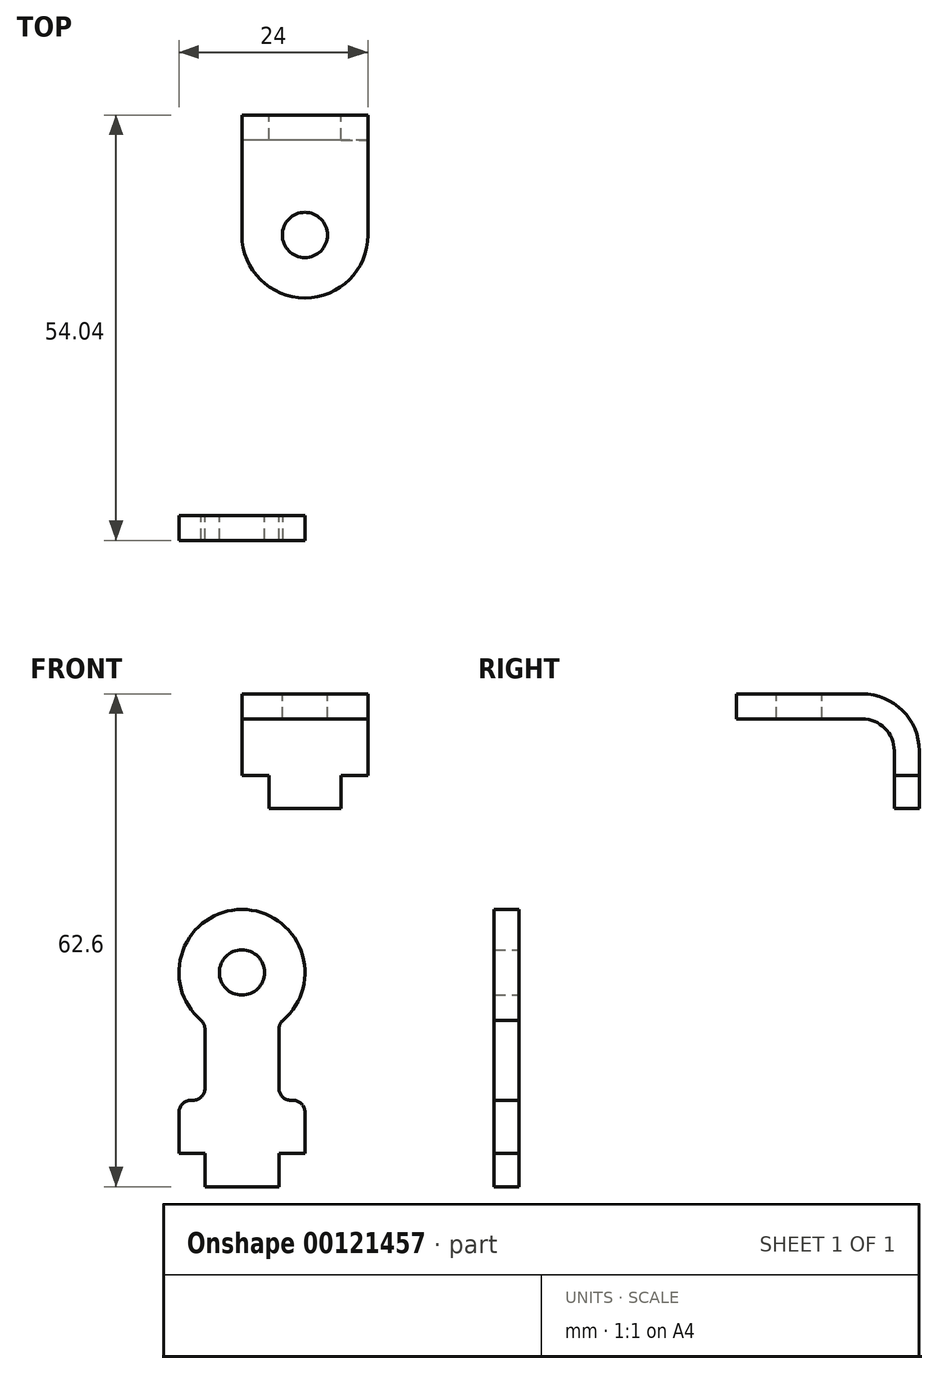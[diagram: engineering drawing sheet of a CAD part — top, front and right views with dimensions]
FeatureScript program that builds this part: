
annotation { "Feature Type Name" : "Feature", "Feature Type Description" : "" }
export const myFeature = defineFeature(function(context is Context, id is Id, definition is map)
    precondition{}
    {
        {
            var Q0;
            Q0=qCreatedBy(makeId("Front.planeOp"),FACE);
            var sketch = newSketch(context, id + "F0", { "sketchPlane" : qUnion([Q0])});
            skCircle(sketch, "E0", {"center": v(0, 0) * mm, "radius": 2.87 * mm});
            skLineSegment(sketch, "E1", {"start": v(-4.7, -7.2) * mm, "end": v(-4.7, -14.72) * mm});
            skLineSegment(sketch, "E2", {"start": v(-6.22, -16.24) * mm, "end": v(-6.48, -16.24) * mm});
            skLineSegment(sketch, "E3", {"start": v(-8, -17.77) * mm, "end": v(-8, -22.99) * mm});
            skLineSegment(sketch, "E4", {"start": v(-8, -22.99) * mm, "end": v(-4.7, -22.99) * mm});
            skLineSegment(sketch, "E5", {"start": v(-4.7, -22.99) * mm, "end": v(-4.7, -27.2) * mm});
            skLineSegment(sketch, "E6", {"start": v(-4.7, -27.2) * mm, "end": v(0, -27.2) * mm});
            skLineSegment(sketch, "E7", {"start": v(-4.7, -7.2) * mm, "end": v(4.7, -7.2) * mm, "construction": true});
            skPoint(sketch, "E8.visualSharp", {"position": v(-4.7, -16.24) * mm});
            skArc(sketch, "E8.filletArc", {"start": v(-6.22, -16.24) * mm, "mid": v(-5.15, -15.8) * mm, "end": v(-4.7, -14.72) * mm});
            skPoint(sketch, "E9.visualSharp", {"position": v(-8, -16.24) * mm});
            skArc(sketch, "E9.filletArc", {"start": v(-6.48, -16.24) * mm, "mid": v(-7.55, -16.69) * mm, "end": v(-8, -17.77) * mm});
            skPoint(sketch, "E10.visualSharp", {"position": v(-4.7, -6.47) * mm});
            skArc(sketch, "E10.filletArc", {"start": v(-4.7, -7.2) * mm, "mid": v(-4.83, -6.59) * mm, "end": v(-5.2, -6.07) * mm});
            skLineSegment(sketch, "E11", {"start": v(-4.7, -14.72) * mm, "end": v(4.7, -14.72) * mm, "construction": true});
            skArc(sketch, "E12.MirrorCS", {"start": v(4.7, -7.2) * mm, "mid": v(4.83, -6.59) * mm, "end": v(5.2, -6.07) * mm});
            skLineSegment(sketch, "E13.MirrorCS", {"start": v(4.7, -7.2) * mm, "end": v(4.7, -14.72) * mm});
            skArc(sketch, "E14.MirrorCS", {"start": v(6.22, -16.24) * mm, "mid": v(5.15, -15.8) * mm, "end": v(4.7, -14.72) * mm});
            skLineSegment(sketch, "E15.MirrorCS", {"start": v(6.22, -16.24) * mm, "end": v(6.48, -16.24) * mm});
            skArc(sketch, "E16.MirrorCS", {"start": v(6.48, -16.24) * mm, "mid": v(7.55, -16.69) * mm, "end": v(8, -17.77) * mm});
            skLineSegment(sketch, "E17.MirrorCS", {"start": v(8, -17.77) * mm, "end": v(8, -22.99) * mm});
            skLineSegment(sketch, "E18.MirrorCS", {"start": v(8, -22.99) * mm, "end": v(4.7, -22.99) * mm});
            skLineSegment(sketch, "E19.MirrorCS", {"start": v(4.7, -22.99) * mm, "end": v(4.7, -27.2) * mm});
            skLineSegment(sketch, "E20.MirrorCS", {"start": v(4.7, -27.2) * mm, "end": v(0, -27.2) * mm});
            skArc(sketch, "E21.trimOffspring", {"start": v(5.2, -6.07) * mm, "mid": v(0, 8) * mm, "end": v(-5.2, -6.07) * mm});
            skSolve(sketch);
        }
        {
            var Q0;
            Q0 = qSketchRegion(id + "F0", true);
            extrude(context, id + "F1", {"entities" : qUnion([Q0]), "depth" : 3.17 * mm});
        }
        {
            var Q0;
            Q0=qCreatedBy(makeId("Right.planeOp"),FACE);
            var sketch = newSketch(context, id + "F2", { "sketchPlane" : qUnion([Q0])});
            skLineSegment(sketch, "E22", {"start": v(50.86, 20.82) * mm, "end": v(47.68, 20.82) * mm});
            skLineSegment(sketch, "E23", {"start": v(47.68, 20.82) * mm, "end": v(47.68, 28.15) * mm});
            skLineSegment(sketch, "E24", {"start": v(43.62, 32.22) * mm, "end": v(27.62, 32.22) * mm});
            skLineSegment(sketch, "E25", {"start": v(27.62, 32.22) * mm, "end": v(27.62, 35.4) * mm});
            skLineSegment(sketch, "E26", {"start": v(27.62, 35.4) * mm, "end": v(43.62, 35.4) * mm});
            skLineSegment(sketch, "E27", {"start": v(50.86, 20.82) * mm, "end": v(50.86, 28.15) * mm});
            skPoint(sketch, "E28.visualSharp", {"position": v(47.68, 32.22) * mm});
            skArc(sketch, "E28.filletArc", {"start": v(47.68, 28.15) * mm, "mid": v(46.5, 31.02) * mm, "end": v(43.62, 32.22) * mm});
            skPoint(sketch, "E29.newPointA", {"position": v(50.86, 32.22) * mm});
            skPoint(sketch, "E29.newPointB", {"position": v(47.68, 35.4) * mm});
            skArc(sketch, "E29.filletArc", {"start": v(50.86, 28.15) * mm, "mid": v(48.74, 33.27) * mm, "end": v(43.62, 35.4) * mm});
            skSolve(sketch);
        }
        {
            var Q0;
            Q0=makeQuery(id+"F2.imprint","IMPRINT",FACE,{"disambiguationData":[TD([[makeQuery(id+"F2.imprint","IMPRINT",EDGE,{"derivedFrom":sQuery(id+"F2.wireOp",EDGE,"E22")}),-1.0]])]});
            extrude(context, id + "F3", {"entities" : qUnion([Q0]), "depth" : 16 * mm});
        }
        {
            var Q0;
            Q0=makeQuery(id+"F3.opExtrude","SWEPT_FACE",FACE,{"disambiguationData":[OSD([sQuery(id+"F2.wireOp",EDGE,"E27")])]});
            var sketch = newSketch(context, id + "F4", { "sketchPlane" : qUnion([Q0])});
            skLineSegment(sketch, "E30", {"start": v(-16, 25.06) * mm, "end": v(-12.57, 25.06) * mm});
            skLineSegment(sketch, "E31", {"start": v(-12.57, 25.06) * mm, "end": v(-12.57, 20.82) * mm});
            skLineSegment(sketch, "E32", {"start": v(-8, 20.82) * mm, "end": v(-8, 28.15) * mm, "construction": true});
            skLineSegment(sketch, "E33.MirrorCS", {"start": v(-3.43, 25.06) * mm, "end": v(-3.43, 20.82) * mm});
            skLineSegment(sketch, "E34.MirrorCS", {"start": v(0, 25.06) * mm, "end": v(-3.43, 25.06) * mm});
            skSolve(sketch);
        }
        {
            var Q0;
            {var subQ0=sQuery(id+"F4.wireOp",EDGE,"E30");Q0=makeQuery(id+"F4.imprint","IMPRINT",FACE,{"disambiguationData":[TD([[makeQuery(id+"F4.imprint","IMPRINT",EDGE,{"derivedFrom":subQ0}),-1.0]])]});}
            var Q1;
            {var subQ0=sQuery(id+"F4.wireOp",EDGE,"E33.MirrorCS");Q1=makeQuery(id+"F4.imprint","IMPRINT",FACE,{"disambiguationData":[TD([[makeQuery(id+"F4.imprint","IMPRINT",EDGE,{"derivedFrom":subQ0}),1.0]])]});}
            extrude(context, id + "F5", {"entities" : qUnion([Q0, Q1]), "operationType" : NewBodyOperationType.REMOVE, "oppositeDirection" : true, "depth" : 25.4 * mm});
        }
        {
            var Q0;
            Q0=makeQuery(id+"F3.opExtrude","SWEPT_FACE",FACE,{"disambiguationData":[OSD([sQuery(id+"F2.wireOp",EDGE,"E26")])]});
            var sketch = newSketch(context, id + "F6", { "sketchPlane" : qUnion([Q0])});
            skCircle(sketch, "E35", {"center": v(8, 35.62) * mm, "radius": 8 * mm});
            skPoint(sketch, "E35.centerSnap0", {"position": v(16, 35.62) * mm});
            skPoint(sketch, "E35.centerSnap1", {"position": v(8, 27.62) * mm});
            skCircle(sketch, "E36", {"center": v(8, 35.62) * mm, "radius": 2.87 * mm});
            skLineSegment(sketch, "E37.bottom", {"start": v(0, 27.62) * mm, "end": v(16, 27.62) * mm});
            skLineSegment(sketch, "E37.top", {"start": v(0, 43.62) * mm, "end": v(16, 43.62) * mm});
            skLineSegment(sketch, "E37.left", {"start": v(0, 27.62) * mm, "end": v(0, 43.62) * mm});
            skLineSegment(sketch, "E37.right", {"start": v(16, 27.62) * mm, "end": v(16, 43.62) * mm});
            skSolve(sketch);
        }
        {
            var Q0;
            {var subQ0=sQuery(id+"F6.wireOp",EDGE,"E37.left");var subQ1=sQuery(id+"F6.wireOp",EDGE,"E35");var subQ2=makeQuery(id+"F6.imprint","INTERSECT",VERTEX,{"derivedFrom":[subQ1,subQ0]});Q0=makeQuery(id+"F6.imprint","IMPRINT",FACE,{"disambiguationData":[TD([[makeQuery(id+"F6.imprint","IMPRINT",EDGE,{"disambiguationData":[TD([[subQ2,-1.0]])],"derivedFrom":subQ1}),-1.0]])]});}
            var Q1;
            {var subQ0=sQuery(id+"F6.wireOp",EDGE,"E37.right");var subQ1=sQuery(id+"F6.wireOp",EDGE,"E35");var subQ2=makeQuery(id+"F6.imprint","INTERSECT",VERTEX,{"derivedFrom":[subQ1,subQ0]});Q1=makeQuery(id+"F6.imprint","IMPRINT",FACE,{"disambiguationData":[TD([[makeQuery(id+"F6.imprint","IMPRINT",EDGE,{"disambiguationData":[TD([[subQ2,1.0]])],"derivedFrom":subQ1}),-1.0]])]});}
            var Q2;
            Q2=makeQuery(id+"F6.imprint","IMPRINT",FACE,{"disambiguationData":[TD([[makeQuery(id+"F6.imprint","IMPRINT",EDGE,{"derivedFrom":sQuery(id+"F6.wireOp",EDGE,"E36")}),1.0]])]});
            extrude(context, id + "F7", {"entities" : qUnion([Q0, Q1, Q2]), "operationType" : NewBodyOperationType.REMOVE, "endBound" : BoundingType.UP_TO_NEXT, "oppositeDirection" : true, "depth" : 25.4 * mm});
        }
    });
